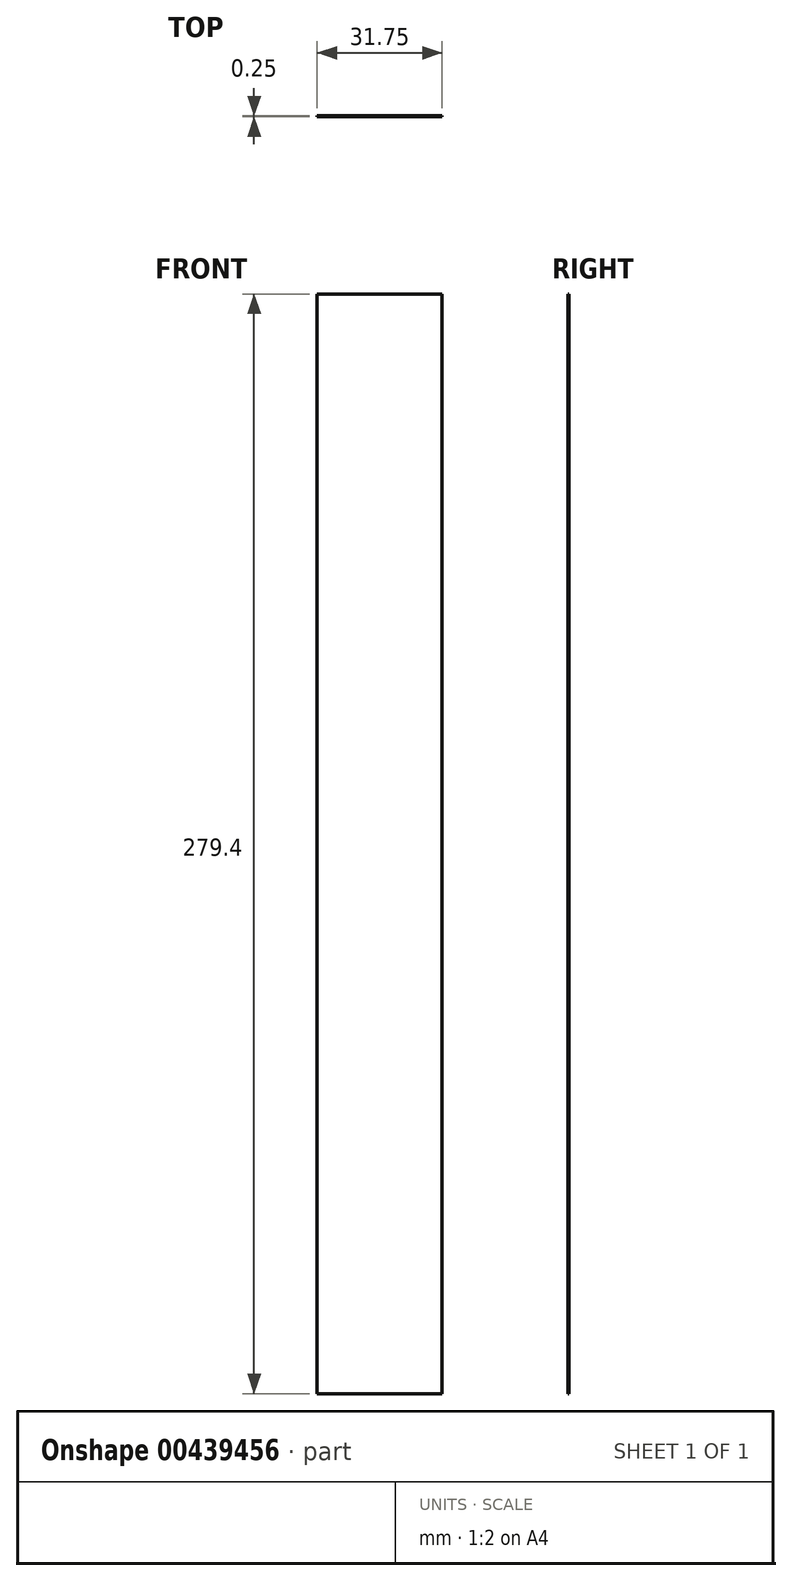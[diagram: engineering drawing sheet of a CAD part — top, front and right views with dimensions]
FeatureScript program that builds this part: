
annotation { "Feature Type Name" : "Feature", "Feature Type Description" : "" }
export const myFeature = defineFeature(function(context is Context, id is Id, definition is map)
    precondition{}
    {
        {
            var Q0;
            Q0=qCreatedBy(makeId("Front.planeOp"),FACE);
            var sketch = newSketch(context, id + "F0", { "sketchPlane" : qUnion([Q0])});
            skLineSegment(sketch, "E0.bottom", {"start": v(-100.18, 0) * mm, "end": v(-68.43, 0) * mm});
            skLineSegment(sketch, "E0.top", {"start": v(-100.18, -279.4) * mm, "end": v(-68.43, -279.4) * mm});
            skLineSegment(sketch, "E0.left", {"start": v(-100.18, 0) * mm, "end": v(-100.18, -279.4) * mm});
            skLineSegment(sketch, "E0.right", {"start": v(-68.43, 0) * mm, "end": v(-68.43, -279.4) * mm});
            skSolve(sketch);
        }
        {
            var Q0;
            Q0=makeQuery(id+"F0.imprint","IMPRINT",FACE,{"disambiguationData":[TD([[makeQuery(id+"F0.imprint","IMPRINT",EDGE,{"derivedFrom":sQuery(id+"F0.wireOp",EDGE,"E0.bottom")}),-1.0]])]});
            extrude(context, id + "F1", {"entities" : qUnion([Q0]), "depth" : 0.25 * mm});
        }
    });
